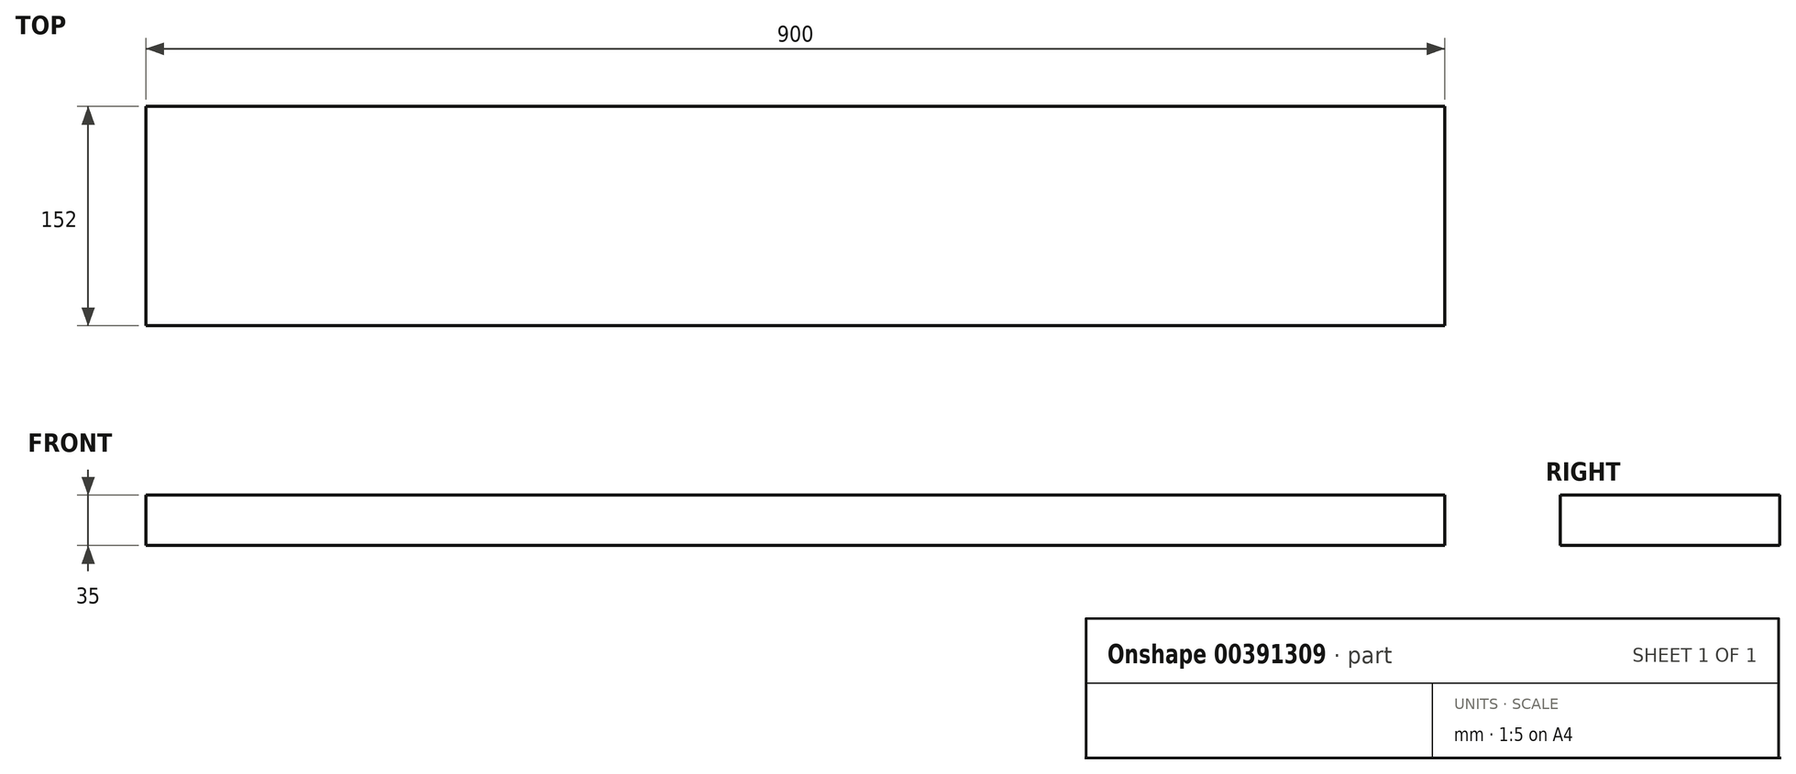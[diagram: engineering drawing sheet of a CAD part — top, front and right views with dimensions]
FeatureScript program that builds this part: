
annotation { "Feature Type Name" : "Feature", "Feature Type Description" : "" }
export const myFeature = defineFeature(function(context is Context, id is Id, definition is map)
    precondition{}
    {
        {
            var Q0;
            Q0=qCreatedBy(makeId("Right.planeOp"),FACE);
            var sketch = newSketch(context, id + "F0", { "sketchPlane" : qUnion([Q0])});
            skLineSegment(sketch, "E0.bottom", {"start": v(73.78, 45.5) * mm, "end": v(-78.22, 45.5) * mm});
            skLineSegment(sketch, "E0.top", {"start": v(73.78, 10.5) * mm, "end": v(-78.22, 10.5) * mm});
            skLineSegment(sketch, "E0.left", {"start": v(73.78, 45.5) * mm, "end": v(73.78, 10.5) * mm});
            skLineSegment(sketch, "E0.right", {"start": v(-78.22, 45.5) * mm, "end": v(-78.22, 10.5) * mm});
            skSolve(sketch);
        }
        {
            var Q0;
            Q0=makeQuery(id+"F0.imprint","IMPRINT",FACE,{"disambiguationData":[TD([[makeQuery(id+"F0.imprint","IMPRINT",EDGE,{"derivedFrom":sQuery(id+"F0.wireOp",EDGE,"E0.bottom")}),1.0]])]});
            extrude(context, id + "F1", {"entities" : qUnion([Q0]), "oppositeDirection" : true, "depth" : 900 * mm});
        }
    });
